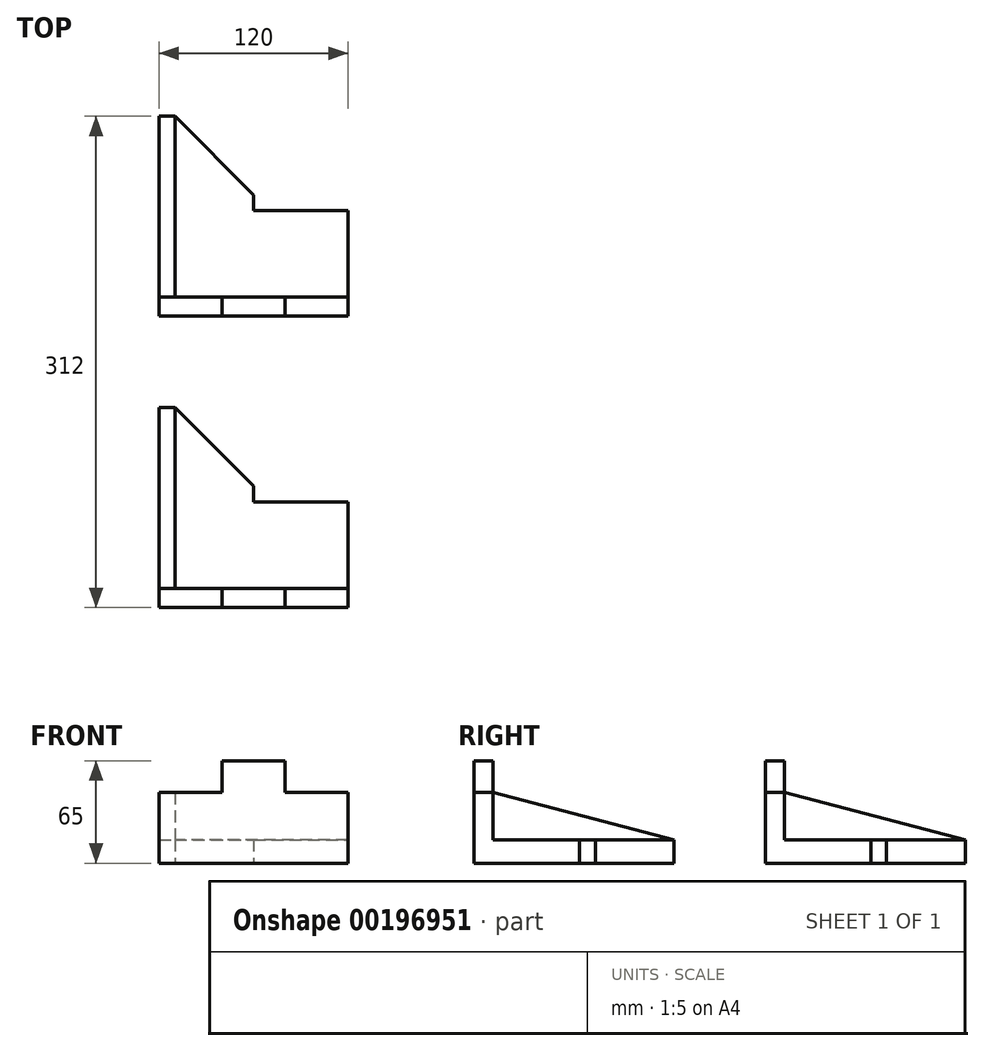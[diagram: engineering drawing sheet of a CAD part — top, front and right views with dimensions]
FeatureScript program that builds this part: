
annotation { "Feature Type Name" : "Feature", "Feature Type Description" : "" }
export const myFeature = defineFeature(function(context is Context, id is Id, definition is map)
    precondition{}
    {
        {
            var Q0;
            Q0=qCreatedBy(makeId("Front.planeOp"),FACE);
            var sketch = newSketch(context, id + "F0", { "sketchPlane" : qUnion([Q0])});
            skLineSegment(sketch, "E0", {"start": v(0, 0) * mm, "end": v(60, 0) * mm});
            skLineSegment(sketch, "E1", {"start": v(60, 0) * mm, "end": v(60, 45) * mm});
            skLineSegment(sketch, "E2", {"start": v(60, 45) * mm, "end": v(20, 45) * mm});
            skLineSegment(sketch, "E3", {"start": v(20, 45) * mm, "end": v(20, 65) * mm});
            skLineSegment(sketch, "E4", {"start": v(20, 65) * mm, "end": v(-20, 65) * mm});
            skLineSegment(sketch, "E5", {"start": v(-20, 65) * mm, "end": v(-20, 45) * mm});
            skLineSegment(sketch, "E6", {"start": v(-20, 45) * mm, "end": v(-60, 45) * mm});
            skLineSegment(sketch, "E7", {"start": v(-60, 45) * mm, "end": v(-60, 0) * mm});
            skLineSegment(sketch, "E8", {"start": v(-60, 0) * mm, "end": v(0, 0) * mm});
            skSolve(sketch);
        }
        {
            var Q0;
            Q0 = qSketchRegion(id + "F0", true);
            extrude(context, id + "F1", {"entities" : qUnion([Q0]), "depth" : 12 * mm});
        }
        {
            var Q0;
            Q0=qCreatedBy(makeId("Top.planeOp"),FACE);
            var sketch = newSketch(context, id + "F2", { "sketchPlane" : qUnion([Q0])});
            skLineSegment(sketch, "E9", {"start": v(0, 0) * mm, "end": v(-60, 0) * mm});
            skLineSegment(sketch, "E10", {"start": v(-60, 0) * mm, "end": v(-60, 115) * mm});
            skLineSegment(sketch, "E11", {"start": v(-60, 115) * mm, "end": v(0, 115) * mm});
            skLineSegment(sketch, "E12", {"start": v(0, 115) * mm, "end": v(0, 55) * mm});
            skLineSegment(sketch, "E13", {"start": v(0, 55) * mm, "end": v(60, 55) * mm});
            skLineSegment(sketch, "E14", {"start": v(60, 55) * mm, "end": v(60, 0) * mm});
            skLineSegment(sketch, "E15", {"start": v(60, 0) * mm, "end": v(0, 0) * mm});
            skSolve(sketch);
        }
        {
            var Q0;
            Q0=makeQuery(id+"F2.imprint","IMPRINT",FACE,{"disambiguationData":[TD([[makeQuery(id+"F2.imprint","IMPRINT",EDGE,{"derivedFrom":sQuery(id+"F2.wireOp",EDGE,"E9")}),-1.0]])]});
            extrude(context, id + "F3", {"entities" : qUnion([Q0]), "operationType" : NewBodyOperationType.ADD, "depth" : 15 * mm});
        }
        {
            var Q0;
            Q0=makeQuery(id+"F3.boolean.opBoolean","MERGE",FACE,{"derivedFrom":[makeQuery(id+"F1.opExtrude","SWEPT_FACE",FACE,{"disambiguationData":[OSD([sQuery(id+"F0.wireOp",EDGE,"E7")])]}),makeQuery(id+"F3.opExtrude","SWEPT_FACE",FACE,{"disambiguationData":[OSD([sQuery(id+"F2.wireOp",EDGE,"E10")])]})]});
            var sketch = newSketch(context, id + "F4", { "sketchPlane" : qUnion([Q0])});
            skLineSegment(sketch, "E16", {"start": v(-115, 15) * mm, "end": v(0, 15) * mm});
            skLineSegment(sketch, "E17", {"start": v(0, 15) * mm, "end": v(0, 45) * mm});
            skLineSegment(sketch, "E18", {"start": v(0, 45) * mm, "end": v(-115, 15) * mm});
            skSolve(sketch);
        }
        {
            var Q0;
            Q0 = qSketchRegion(id + "F4", true);
            extrude(context, id + "F5", {"entities" : qUnion([Q0]), "operationType" : NewBodyOperationType.ADD, "oppositeDirection" : true, "depth" : 10 * mm});
        }
        {
            var Q0;
            Q0=makeQuery(id+"F3.opExtrude","SWEPT_EDGE",EDGE,{"disambiguationData":[OSD([sQuery(id+"F2.wireOp",EDGE,"E11"),sQuery(id+"F2.wireOp",EDGE,"E12")])]});
            chamfer(context, id + "F6", {"entities" : qUnion([Q0]), "width" : 50 * mm, "tangentPropagation" : true});
        }
        {
            var Q0;
            Q0=makeQuery(id+"F1.opExtrude","SWEPT_BODY",BODY,{"disambiguationData":[OSD([sQuery(id+"F0.wireOp",EDGE,"E0"),sQuery(id+"F0.wireOp",EDGE,"E1"),sQuery(id+"F0.wireOp",EDGE,"E2"),sQuery(id+"F0.wireOp",EDGE,"E3"),sQuery(id+"F0.wireOp",EDGE,"E4"),sQuery(id+"F0.wireOp",EDGE,"E5"),sQuery(id+"F0.wireOp",EDGE,"E6"),sQuery(id+"F0.wireOp",EDGE,"E7"),sQuery(id+"F0.wireOp",EDGE,"E8")])]});
            transform(context, id + "F7", {"entities" : qUnion([Q0]), "transformType" : TransformType.TRANSLATION_3D, "dx" : 0 * mm, "dy" : 185 * mm, "dz" : 0 * mm, "makeCopy" : true});
        }
    });
